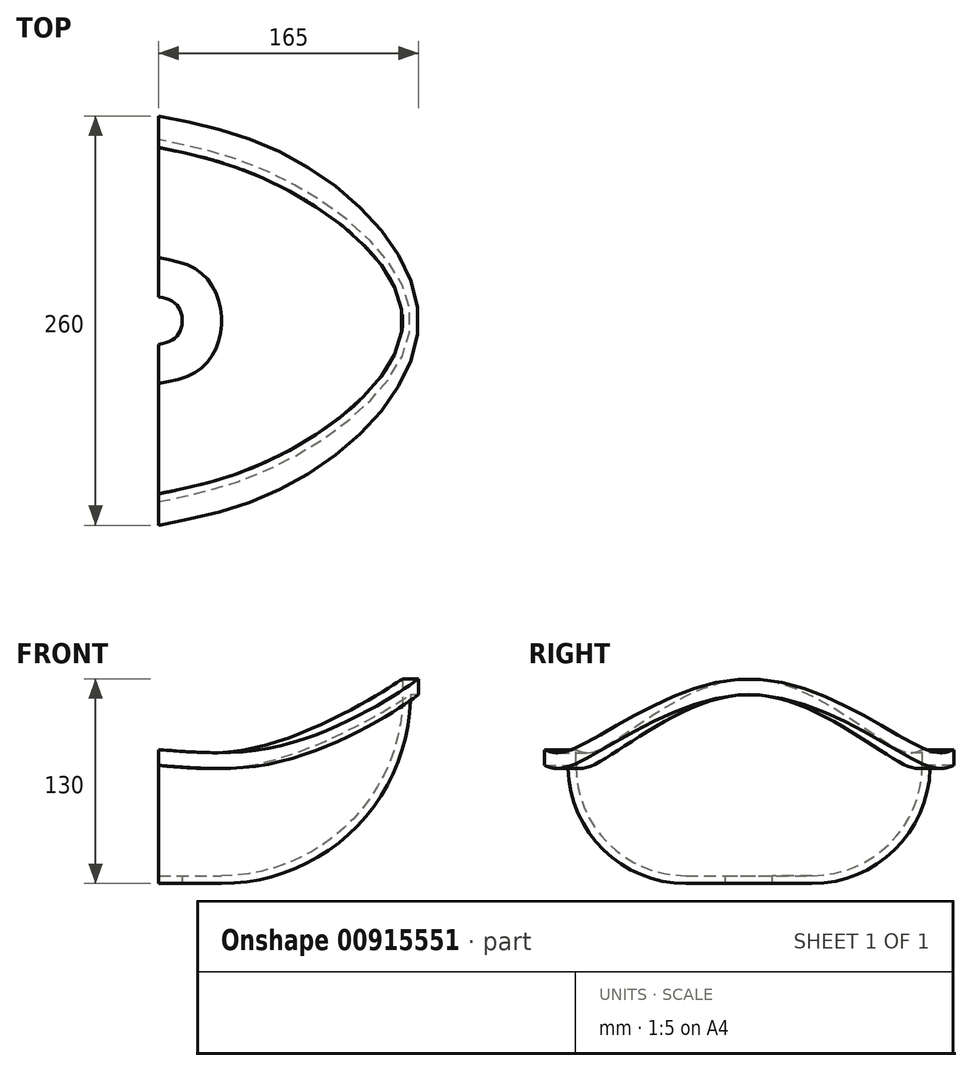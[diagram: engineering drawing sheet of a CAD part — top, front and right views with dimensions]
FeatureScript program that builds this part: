
annotation { "Feature Type Name" : "Feature", "Feature Type Description" : "" }
export const myFeature = defineFeature(function(context is Context, id is Id, definition is map)
    precondition{}
    {
        {
            var Q0;
            Q0=qCreatedBy(makeId("Front.planeOp"),FACE);
            var sketch = newSketch(context, id + "F0", { "sketchPlane" : qUnion([Q0])});
            skLineSegment(sketch, "E0.bottom", {"start": v(165, 120) * mm, "end": v(160, 120) * mm});
            skLineSegment(sketch, "E0.top", {"start": v(165, 130) * mm, "end": v(155, 130) * mm});
            skLineSegment(sketch, "E0.left", {"start": v(165, 120) * mm, "end": v(165, 130) * mm});
            skLineSegment(sketch, "E0.right", {"start": v(155, 120) * mm, "end": v(155, 130) * mm});
            skArc(sketch, "E1", {"start": v(40, 0) * mm, "mid": v(124.85, 35.15) * mm, "end": v(160, 120) * mm});
            skArc(sketch, "E2", {"start": v(40, 5) * mm, "mid": v(121.32, 38.68) * mm, "end": v(155, 120) * mm});
            skLineSegment(sketch, "E3.bottom", {"start": v(40, 0) * mm, "end": v(15, 0) * mm});
            skLineSegment(sketch, "E3.top", {"start": v(40, 5) * mm, "end": v(15, 5) * mm});
            skLineSegment(sketch, "E3.left", {"start": v(40, 0) * mm, "end": v(40, 5) * mm, "construction": true});
            skLineSegment(sketch, "E3.right", {"start": v(15, 0) * mm, "end": v(15, 5) * mm});
            skLineSegment(sketch, "E4", {"start": v(0, 0) * mm, "end": v(0, 50) * mm, "construction": true});
            skSolve(sketch);
        }
        {
            var Q0;
            Q0=sQuery(id+"F0.wireOp",EDGE,"E4");
            cPlane(context, id + "F1", {"entities" : qUnion([Q0]), "cplaneType" : CPlaneType.LINE_ANGLE, "offset" : 25 * mm, "angle" : 30 * degree, "oppositeDirection" : true, "width" : 150 * mm, "height" : 150 * mm});
        }
        {
            var Q0;
            Q0=qCreatedBy(id+"F1.planeOp",FACE);
            var sketch = newSketch(context, id + "F2", { "sketchPlane" : qUnion([Q0])});
            skLineSegment(sketch, "E5.bottom", {"start": v(130, 75) * mm, "end": v(115, 75) * mm});
            skLineSegment(sketch, "E5.top", {"start": v(130, 85) * mm, "end": v(110, 85) * mm});
            skLineSegment(sketch, "E5.left", {"start": v(130, 75) * mm, "end": v(130, 85) * mm});
            skLineSegment(sketch, "E5.right", {"start": v(110, 75) * mm, "end": v(110, 85) * mm});
            skArc(sketch, "E6", {"start": v(40, 0) * mm, "mid": v(93.03, 21.97) * mm, "end": v(115, 75) * mm});
            skArc(sketch, "E7", {"start": v(40, 5) * mm, "mid": v(89.5, 25.5) * mm, "end": v(110, 75) * mm});
            skLineSegment(sketch, "E8.bottom", {"start": v(40, 0) * mm, "end": v(15, 0) * mm});
            skLineSegment(sketch, "E8.top", {"start": v(40, 5) * mm, "end": v(15, 5) * mm});
            skLineSegment(sketch, "E8.left", {"start": v(40, 0) * mm, "end": v(40, 5) * mm, "construction": true});
            skLineSegment(sketch, "E8.right", {"start": v(15, 0) * mm, "end": v(15, 5) * mm});
            skLineSegment(sketch, "E9", {"start": v(0, 0) * mm, "end": v(0, 50) * mm, "construction": true});
            skSolve(sketch);
        }
        {
            var Q0;
            Q0=sQuery(id+"F2.wireOp",EDGE,"E9");
            cPlane(context, id + "F3", {"entities" : qUnion([Q0]), "cplaneType" : CPlaneType.LINE_ANGLE, "offset" : 25 * mm, "angle" : 150 * degree, "oppositeDirection" : true, "width" : 150 * mm, "height" : 150 * mm});
        }
        {
            var Q0;
            Q0=qCreatedBy(id+"F3.planeOp",FACE);
            var sketch = newSketch(context, id + "F4", { "sketchPlane" : qUnion([Q0])});
            skLineSegment(sketch, "E10.bottom", {"start": v(130, 75) * mm, "end": v(115, 75) * mm});
            skLineSegment(sketch, "E10.top", {"start": v(130, 85) * mm, "end": v(110, 85) * mm});
            skLineSegment(sketch, "E10.left", {"start": v(130, 75) * mm, "end": v(130, 85) * mm});
            skLineSegment(sketch, "E10.right", {"start": v(110, 75) * mm, "end": v(110, 85) * mm});
            skArc(sketch, "E11", {"start": v(40, 0) * mm, "mid": v(93.03, 21.97) * mm, "end": v(115, 75) * mm});
            skArc(sketch, "E12", {"start": v(40, 5) * mm, "mid": v(89.5, 25.5) * mm, "end": v(110, 75) * mm});
            skLineSegment(sketch, "E13.bottom", {"start": v(40, 0) * mm, "end": v(15, 0) * mm});
            skLineSegment(sketch, "E13.top", {"start": v(40, 5) * mm, "end": v(15, 5) * mm});
            skLineSegment(sketch, "E13.left", {"start": v(40, 0) * mm, "end": v(40, 5) * mm, "construction": true});
            skLineSegment(sketch, "E13.right", {"start": v(15, 0) * mm, "end": v(15, 5) * mm});
            skLineSegment(sketch, "E14", {"start": v(0, 0) * mm, "end": v(0, 50) * mm, "construction": true});
            skSolve(sketch);
        }
        {
            var Q0;
            Q0=qCreatedBy(makeId("Right.planeOp"),FACE);
            var sketch = newSketch(context, id + "F5", { "sketchPlane" : qUnion([Q0])});
            skLineSegment(sketch, "E15.bottom", {"start": v(130, 75) * mm, "end": v(115, 75) * mm});
            skLineSegment(sketch, "E15.top", {"start": v(130, 85) * mm, "end": v(110, 85) * mm});
            skLineSegment(sketch, "E15.left", {"start": v(130, 75) * mm, "end": v(130, 85) * mm});
            skLineSegment(sketch, "E15.right", {"start": v(110, 75) * mm, "end": v(110, 85) * mm});
            skArc(sketch, "E16", {"start": v(40, 0) * mm, "mid": v(93.03, 21.97) * mm, "end": v(115, 75) * mm});
            skArc(sketch, "E17", {"start": v(40, 5) * mm, "mid": v(89.5, 25.5) * mm, "end": v(110, 75) * mm});
            skLineSegment(sketch, "E18.bottom", {"start": v(40, 0) * mm, "end": v(15, 0) * mm});
            skLineSegment(sketch, "E18.top", {"start": v(40, 5) * mm, "end": v(15, 5) * mm});
            skLineSegment(sketch, "E18.left", {"start": v(40, 0) * mm, "end": v(40, 5) * mm, "construction": true});
            skLineSegment(sketch, "E18.right", {"start": v(15, 0) * mm, "end": v(15, 5) * mm});
            skLineSegment(sketch, "E19", {"start": v(0, 0) * mm, "end": v(0, 50) * mm, "construction": true});
            skSolve(sketch);
        }
        {
            var Q0;
            Q0=sQuery(id+"F5.wireOp",EDGE,"E19");
            cPlane(context, id + "F6", {"entities" : qUnion([Q0]), "cplaneType" : CPlaneType.LINE_ANGLE, "offset" : 25 * mm, "angle" : 180 * degree, "width" : 150 * mm, "height" : 150 * mm});
        }
        {
            var Q0;
            Q0=qCreatedBy(id+"F6.planeOp",FACE);
            var sketch = newSketch(context, id + "F7", { "sketchPlane" : qUnion([Q0])});
            skLineSegment(sketch, "E20.bottom", {"start": v(130, 75) * mm, "end": v(115, 75) * mm});
            skLineSegment(sketch, "E20.top", {"start": v(130, 85) * mm, "end": v(110, 85) * mm});
            skLineSegment(sketch, "E20.left", {"start": v(130, 75) * mm, "end": v(130, 85) * mm});
            skLineSegment(sketch, "E20.right", {"start": v(110, 75) * mm, "end": v(110, 85) * mm});
            skArc(sketch, "E21", {"start": v(40, 0) * mm, "mid": v(93.03, 21.97) * mm, "end": v(115, 75) * mm});
            skArc(sketch, "E22", {"start": v(40, 5) * mm, "mid": v(89.5, 25.5) * mm, "end": v(110, 75) * mm});
            skLineSegment(sketch, "E23.bottom", {"start": v(40, 0) * mm, "end": v(15, 0) * mm});
            skLineSegment(sketch, "E23.top", {"start": v(40, 5) * mm, "end": v(15, 5) * mm});
            skLineSegment(sketch, "E23.left", {"start": v(40, 0) * mm, "end": v(40, 5) * mm, "construction": true});
            skLineSegment(sketch, "E23.right", {"start": v(15, 0) * mm, "end": v(15, 5) * mm});
            skLineSegment(sketch, "E24", {"start": v(0, 0) * mm, "end": v(0, 50) * mm, "construction": true});
            skSolve(sketch);
        }
        {
            var Q0;
            Q0 = qSketchRegion(id + "F7", true);
            var Q1;
            Q1 = qSketchRegion(id + "F4", true);
            var Q2;
            Q2 = qSketchRegion(id + "F0", true);
            var Q3;
            Q3 = qSketchRegion(id + "F2", true);
            var Q4;
            Q4 = qSketchRegion(id + "F5", true);
            loft(context, id + "F8", {"sheetProfilesArray" : [{ "sheetProfileEntities" : qUnion([Q0]) }, { "sheetProfileEntities" : qUnion([Q1]) }, { "sheetProfileEntities" : qUnion([Q2]) }, { "sheetProfileEntities" : qUnion([Q3]) }, { "sheetProfileEntities" : qUnion([Q4]) }]});
        }
    });
